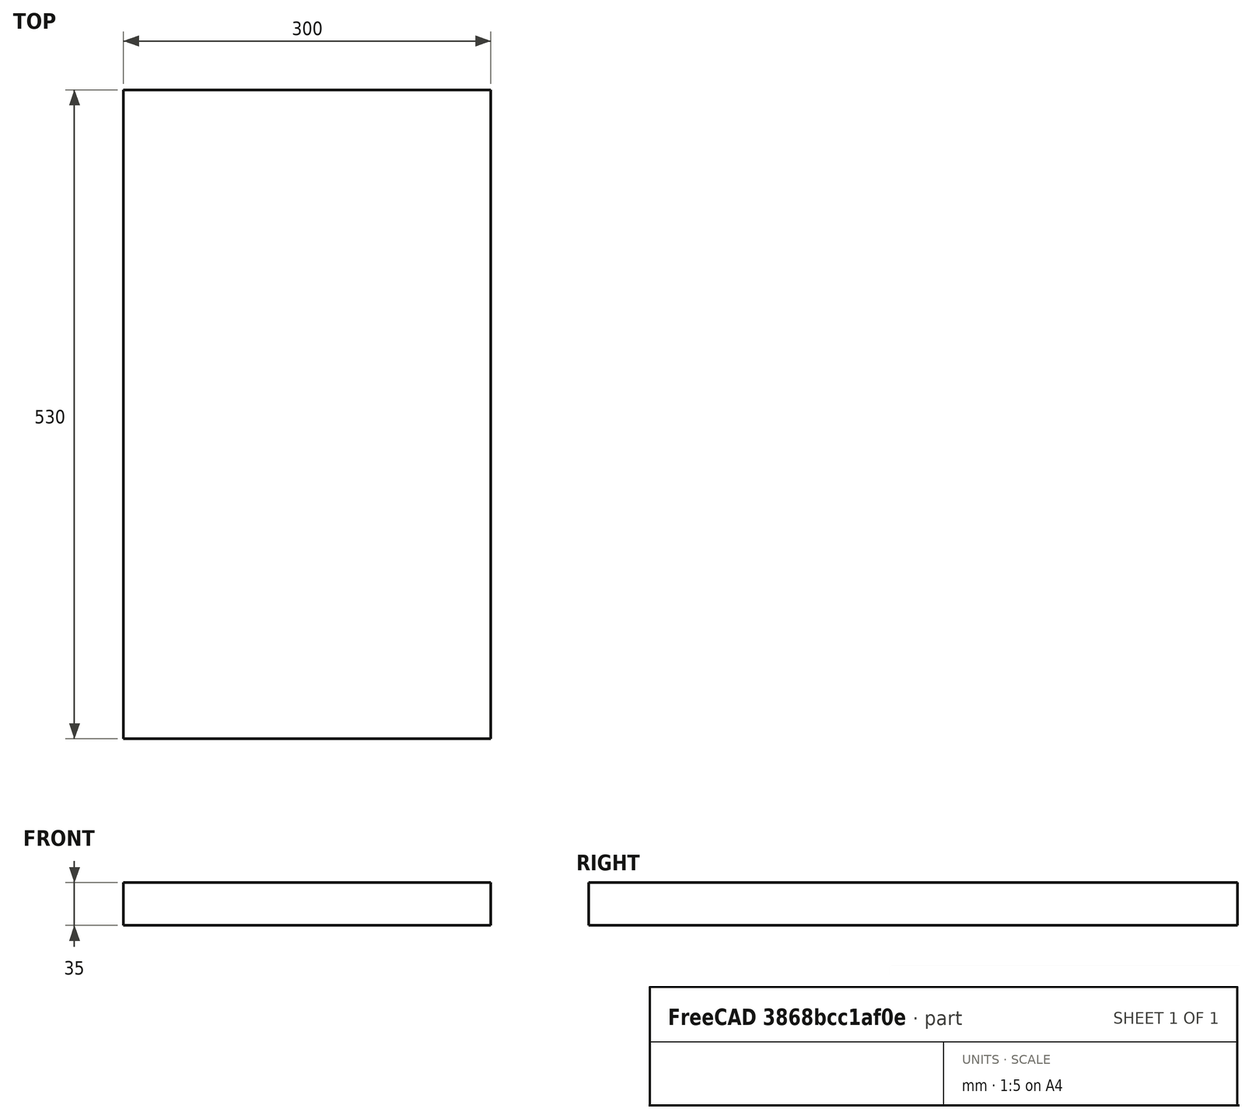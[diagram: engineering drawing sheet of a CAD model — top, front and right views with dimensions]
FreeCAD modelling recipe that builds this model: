
FCSTD DOCUMENT  (FreeCAD 0.18R4 (GitTag))
Label: top_plate
License: All rights reserved
LicenseURL: http://en.wikipedia.org/wiki/All_rights_reserved
objects: Sketcher::SketchObject×1, PartDesign::Pad×1, PartDesign::Body×1
note: 4 computed .brp shape members not serialized (recipe doc carries the construction recipe); baked Part::Feature solids carry a one-line shape summary decoded from their .brp

FEATURE [Sketcher::SketchObject] Sketch
  MapMode = 5
  Placement = pos=(0,0,0) rot=(1,0,0;1.5708rad)
  Support = -> [XZ_Plane]
  sketch-geometry (4):
    g0: LineSegment StartX=0 StartY=0 StartZ=0 EndX=-300 EndY=0 EndZ=0
    g1: LineSegment StartX=-300 StartY=0 StartZ=0 EndX=-300 EndY=35 EndZ=0
    g2: LineSegment StartX=-300 StartY=35 StartZ=0 EndX=0 EndY=35 EndZ=0
    g3: LineSegment StartX=0 StartY=35 StartZ=0 EndX=0 EndY=0 EndZ=0
  constraints (11):
    c: Coincident(g0,g1)
    c: Coincident(g1,g2)
    c: Coincident(g2,g3)
    c: Coincident(g3,g0)
    c: Horizontal(g0)
    c: Horizontal(g2)
    c: Vertical(g1)
    c: Vertical(g3)
    c: Coincident(g0,g-1)
    c: DistanceX(g0,g0) = 300
    c: DistanceY(g3,g3) = 35
FEATURE [PartDesign::Pad] Pad
  Length = 530
  Length2 = 100
  Placement = pos=(0,0,0) rot=(1,0,0;1.5708rad)
  Profile = -> Sketch
  Type = 0
FEATURE [PartDesign::Body] Body
  Group = -> [Sketch,Pad]
  Origin = -> Origin
  Tip = -> Pad
